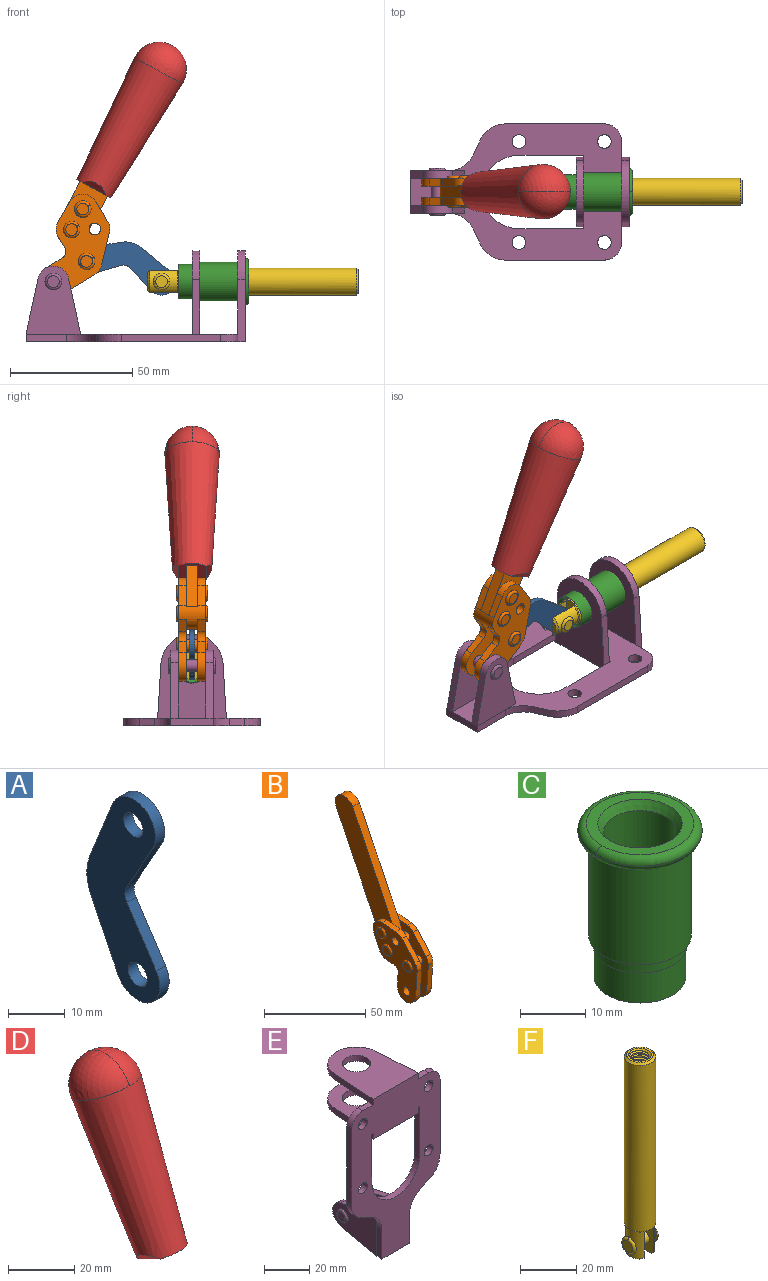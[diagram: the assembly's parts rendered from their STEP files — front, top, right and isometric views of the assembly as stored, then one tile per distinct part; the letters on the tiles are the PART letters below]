
ASSEMBLY  parts=6 mates=6
PART A: 12 faces, bbox 2.3x18.2x42.8 mm
  f0: cylinder r=2.4mm len=4.8mm, axis (1,0,0), area 34.9mm2, adj f4,f11
  f1: cylinder r=10.41mm len=8.47mm, axis (1,0,0), area 20.2mm2, adj f4,f9,f10,f11
  f2: cylinder r=3.05mm len=3.16mm, axis (1,0,0), area 7.7mm2, adj f4,f6,f7,f11
  f3: cylinder r=2.4mm len=4.8mm, axis (1,0,0), area 34.9mm2, adj f4,f11
  f4: plane 42.81x18.23mm, normal (-1,0,0), area 414.1mm2, adj f0,f1,f2,f3,f5,f6,f7,f8
  f5: cylinder r=5.54mm len=10.67mm, axis (1,0,0), area 41.8mm2, adj f4,f6,f10,f11
  f6: plane 11.66x6.53mm, normal (0,-0.87,-0.49), area 30.9mm2, adj f2,f4,f5,f11
  f7: plane 11.17x7.33mm, normal (0,-0.84,0.55), area 30.9mm2, adj f2,f4,f8,f11
  f8: cylinder r=5.54mm len=10.51mm, axis (1,0,0), area 41.8mm2, adj f4,f7,f9,f11
  f9: plane 13.67x6.67mm, normal (0,0.9,-0.44), area 35.1mm2, adj f1,f4,f8,f11
  f10: plane 14.1x5.7mm, normal (0,0.93,0.37), area 35.1mm2, adj f1,f4,f5,f11
  f11: plane 42.81x18.23mm, normal (1,0,0), area 414.1mm2, adj f0,f1,f2,f3,f5,f6,f7,f8
PART B: 59 faces, bbox 12.9x60.2x99.6 mm
  f0: torus R=2.39mm, axis (-1,0,0), area 14.9mm2, adj f20,f43,f51
  f1: torus R=2.39mm, axis (-1,0,0), area 14.9mm2, adj f19,f42,f51
  f2: torus R=2.39mm, axis (-1,0,0), area 14.9mm2, adj f18,f35,f51
  f3: torus R=2.39mm, axis (-1,0,0), area 14.9mm2, adj f14,f17,f23
  f4: torus R=2.39mm, axis (-1,0,0), area 14.9mm2, adj f13,f16,f23
  f5: torus R=2.39mm, axis (-1,0,0), area 14.9mm2, adj f12,f15,f23
  f6: cylinder r=2.39mm len=4.78mm, axis (1,0,0), area 46.5mm2, adj f48,f50,f51
  f7: cylinder r=2.39mm len=4.78mm, axis (1,0,0), area 46.5mm2, adj f50,f51
  f8: cylinder r=6.35mm len=12.68mm, axis (1,0,0), area 61.8mm2, adj f38,f39,f50,f51
  f9: cylinder r=2.39mm len=4.78mm, axis (-1,0,0), area 70.5mm2, adj f46,f50
  f10: cylinder r=2.39mm len=4.78mm, axis (-1,0,0), area 46.5mm2, adj f23,f45,f46
  f11: cylinder r=2.39mm len=4.78mm, axis (-1,0,0), area 46.5mm2, adj f23,f46
  f12: plane 4.78x4.78mm, normal (1,0,0), area 17.9mm2, adj f5,f15
  f13: plane 4.78x4.78mm, normal (1,0,0), area 17.9mm2, adj f4,f16
  f14: plane 4.78x4.78mm, normal (1,0,0), area 17.9mm2, adj f3,f17
  f15: torus R=2.39mm, axis (-1,0,0), area 14.9mm2, adj f5,f12,f23
  f16: torus R=2.39mm, axis (-1,0,0), area 14.9mm2, adj f4,f13,f23
  f17: torus R=2.39mm, axis (-1,0,0), area 14.9mm2, adj f3,f14,f23
  f18: plane 4.78x4.78mm, normal (-1,0,0), area 17.9mm2, adj f2,f35
  f19: plane 4.78x4.78mm, normal (-1,0,0), area 17.9mm2, adj f1,f42
  f20: plane 4.78x4.78mm, normal (-1,0,0), area 17.9mm2, adj f0,f43
  f21: plane 2.26x0.2mm, normal (1,0,0), area 0.2mm2, adj f31,f44
  f22: plane 2.26x0.2mm, normal (-1,0,0), area 0.2mm2, adj f41,f44
  f23: plane 39.37x30.77mm, normal (1,0,0), area 565.5mm2, adj f3,f4,f5,f10,f11,f15,f16,f17
  f24: cylinder r=6.1mm len=4.15mm, axis (-1,0,0), area 14.7mm2, adj f23,f25,f32,f46
  f25: plane 10.25x9.01mm, normal (0,-0.75,0.66), area 42.3mm2, adj f23,f24,f26,f46
  f26: cylinder r=6.35mm len=4.64mm, axis (-1,0,0), area 15.6mm2, adj f23,f25,f27,f46
  f27: plane 15.84x3.1mm, normal (0,-1,-0.07), area 49.2mm2, adj f23,f26,f28,f46
  f28: cylinder r=6.35mm len=12.68mm, axis (-1,0,0), area 61.8mm2, adj f23,f27,f29,f46
  f29: plane 8.11x3.1mm, normal (0,1,0.07), area 25.2mm2, adj f23,f28,f30,f46
  f30: cylinder r=3.05mm len=3.25mm, axis (-1,0,0), area 14.8mm2, adj f23,f29,f31,f46
  f31: plane 5.99x3.1mm, normal (0,0.07,-1), area 18.6mm2, adj f21,f23,f30,f44,f46
  f32: plane 9.5x3.1mm, normal (0,-0.07,1), area 29.5mm2, adj f23,f24,f33,f46,f47
  f33: cylinder r=6.1mm len=8.63mm, axis (-1,0,0), area 39.1mm2, adj f23,f32,f34,f47
  f34: plane 8.65x3.96mm, normal (0,0.91,-0.42), area 29.5mm2, adj f23,f33,f44,f47
  f35: torus R=2.39mm, axis (-1,0,0), area 14.9mm2, adj f2,f18,f51
  f36: plane 10.25x9.01mm, normal (0,-0.75,0.66), area 42.3mm2, adj f37,f49,f50,f51
  f37: cylinder r=6.35mm len=4.64mm, axis (1,0,0), area 15.6mm2, adj f36,f38,f50,f51
  f38: plane 15.84x3.1mm, normal (0,-1,-0.07), area 49.2mm2, adj f8,f37,f50,f51
  f39: plane 8.11x3.1mm, normal (0,1,0.07), area 25.2mm2, adj f8,f40,f50,f51
  f40: cylinder r=3.05mm len=3.25mm, axis (1,0,0), area 14.8mm2, adj f39,f41,f50,f51
  f41: plane 5.99x3.1mm, normal (0,0.07,-1), area 18.6mm2, adj f22,f40,f44,f50,f51
  f42: torus R=2.39mm, axis (-1,0,0), area 14.9mm2, adj f1,f19,f51
  f43: torus R=2.39mm, axis (-1,0,0), area 14.9mm2, adj f0,f20,f51
  f44: cylinder r=6.35mm len=12.12mm, axis (-1,0,0), area 128.9mm2, adj f21,f22,f23,f31,f34,f41,f46,f47
  f45: plane 2.65x1.35mm, normal (1,0,0), area 1mm2, adj f10,f55
  f46: plane 39.08x20.42mm, normal (-1,0,0), area 412.5mm2, adj f9,f10,f11,f24,f25,f26,f27,f28
  f47: plane 77.62x39.82mm, normal (1,0,0), area 850mm2, adj f32,f33,f34,f44,f53,f54,f55
  f48: plane 2.65x1.35mm, normal (-1,0,0), area 1mm2, adj f6,f55
  f49: cylinder r=6.1mm len=4.15mm, axis (1,0,0), area 14.7mm2, adj f36,f50,f51,f56
  f50: plane 39.08x20.42mm, normal (1,0,0), area 412.5mm2, adj f6,f7,f8,f9,f36,f37,f38,f39
  f51: plane 39.37x30.77mm, normal (-1,0,0), area 565.5mm2, adj f0,f1,f2,f6,f7,f8,f35,f36
  f52: plane 8.65x3.96mm, normal (0,0.91,-0.42), area 29.5mm2, adj f44,f51,f57,f58
  f53: plane 68.49x33.4mm, normal (0,0.9,-0.44), area 358.1mm2, adj f44,f47,f54,f58
  f54: cylinder r=6.35mm len=12.06mm, axis (1,0,0), area 93.7mm2, adj f47,f53,f55,f58
  f55: plane 68.49x33.4mm, normal (0,-0.9,0.44), area 358.1mm2, adj f44,f45,f46,f47,f48,f50,f54,f58
  f56: plane 9.5x3.1mm, normal (0,-0.07,1), area 29.5mm2, adj f49,f50,f51,f57,f58
  f57: cylinder r=6.1mm len=8.63mm, axis (1,0,0), area 39.1mm2, adj f51,f52,f56,f58
  f58: plane 77.62x39.82mm, normal (-1,0,0), area 850mm2, adj f44,f52,f53,f54,f55,f56,f57
PART C: 15 faces, bbox 20.6x20.6x28.7 mm
  f0: torus R=8.26mm, axis (0,0,1), area 56.8mm2, adj f1,f10,f12
  f1: torus R=8.26mm, axis (0,0,1), area 56.8mm2, adj f0,f6,f13
  f2: cylinder r=5.59mm len=25.91mm, axis (0,0,1), area 909.6mm2, adj f3,f4
  f3: cone r=6.86mm half-angle=45deg, axis (0,0,-1), area 70.2mm2, adj f2,f14
  f4: cone r=6.47mm half-angle=30deg, axis (0,0,1), area 66.7mm2, adj f2,f13
  f5: cylinder r=7.04mm len=14.07mm, axis (0,0,1), area 252.6mm2, adj f11,f14
  f6: torus R=8.26mm, axis (0,0,1), area 56.8mm2, adj f1,f12,f13
  f7: cylinder r=7.16mm len=14.33mm, axis (0,0,1), area 91.5mm2, adj f9,f11
  f8: cylinder r=7.86mm len=18.42mm, axis (0,0,1), area 909.6mm2, adj f9,f10
  f9: plane 15.72x15.72mm, normal (0,0,-1), area 33mm2, adj f7,f8
  f10: plane 16.51x16.51mm, normal (0,0,-1), area 19.9mm2, adj f0,f8,f12
  f11: plane 14.33x14.33mm, normal (0,0,-1), area 5.7mm2, adj f5,f7
  f12: torus R=8.26mm, axis (0,0,1), area 56.8mm2, adj f0,f6,f10
  f13: plane 16.51x16.51mm, normal (0,0,1), area 82.7mm2, adj f1,f4,f6
  f14: plane 14.07x14.07mm, normal (0,0,-1), area 7.8mm2, adj f3,f5
PART D: 11 faces, bbox 22.3x42.6x64.5 mm
  f0: sphere r=11.13mm, area 411.4mm2, adj f1,f8
  f1: cone r=11.11mm half-angle=3.3deg, axis (0,0.44,0.9), area 3251.8mm2, adj f0,f7,f8,f9,f10
  f2: cylinder r=6.16mm len=11.7mm, axis (1,0,0), area 89.5mm2, adj f3,f4,f5,f6
  f3: plane 60.23x36.75mm, normal (-1,0,0), area 763.6mm2, adj f2,f4,f6,f10
  f4: plane 51.37x25.05mm, normal (0,0.9,-0.44), area 264.2mm2, adj f2,f3,f5,f10
  f5: plane 60.23x36.75mm, normal (1,0,0), area 763.6mm2, adj f2,f4,f6,f10
  f6: plane 51.37x25.05mm, normal (0,-0.9,0.44), area 264.2mm2, adj f2,f3,f5,f10
  f7: plane 9.95x5.95mm, normal (0.71,-0.31,-0.64), area 25.8mm2, adj f1,f10
  f8: sphere r=11.13mm, area 411.4mm2, adj f0,f1
  f9: plane 9.95x5.95mm, normal (-0.71,-0.31,-0.64), area 25.8mm2, adj f1,f10
  f10: plane 14.27x11.38mm, normal (0,-0.44,-0.9), area 106.7mm2, adj f1,f3,f4,f5,f6,f7,f9
PART E: 55 faces, bbox 55.7x37.4x89.8 mm
  f0: torus R=2.41mm, axis (-1,0,0), area 15mm2, adj f11,f15,f25
  f1: torus R=2.41mm, axis (-1,0,0), area 15mm2, adj f10,f12,f22
  f2: cylinder r=2.78mm len=5.56mm, axis (0,-1,0), area 54.2mm2, adj f30,f54
  f3: cylinder r=14.99mm len=29.97mm, axis (0,-1,0), area 145.9mm2, adj f30,f49,f53,f54
  f4: cylinder r=2.78mm len=5.56mm, axis (0,-1,0), area 54.2mm2, adj f30,f54
  f5: cylinder r=2.78mm len=5.56mm, axis (0,-1,0), area 54.2mm2, adj f30,f54
  f6: cylinder r=2.78mm len=5.56mm, axis (0,-1,0), area 54.2mm2, adj f30,f54
  f7: cylinder r=6.35mm len=12.7mm, axis (0,0,1), area 123.6mm2, adj f27,f51
  f8: cylinder r=6.35mm len=12.7mm, axis (0,0,-1), area 124.7mm2, adj f21,f35
  f9: cylinder r=2.41mm len=11.18mm, axis (-1,0,0), area 169.4mm2, adj f16,f19
  f10: plane 4.83x4.83mm, normal (1,0,0), area 18.3mm2, adj f1,f12
  f11: plane 4.83x4.83mm, normal (-1,0,0), area 18.3mm2, adj f0,f15
  f12: torus R=2.41mm, axis (-1,0,0), area 15mm2, adj f1,f10,f22
  f13: cylinder r=6.35mm len=12.41mm, axis (1,0,0), area 53.4mm2, adj f18,f19,f22,f23
  f14: cylinder r=6.35mm len=12.41mm, axis (-1,0,0), area 53.4mm2, adj f16,f17,f24,f25
  f15: torus R=2.41mm, axis (-1,0,0), area 15mm2, adj f0,f11,f25
  f16: plane 27.86x22.35mm, normal (1,0,0), area 425.4mm2, adj f9,f14,f17,f24,f30
  f17: plane 22.86x4.97mm, normal (0,0.21,0.98), area 72.5mm2, adj f14,f16,f25,f30
  f18: plane 22.86x4.97mm, normal (0,0.21,0.98), area 72.5mm2, adj f13,f19,f22,f30
  f19: plane 27.86x22.35mm, normal (-1,0,0), area 425.4mm2, adj f9,f13,f18,f23,f30
  f20: cylinder r=12.7mm len=25.35mm, axis (0,0,-1), area 119.8mm2, adj f21,f34,f35,f36
  f21: plane 34.21x28.07mm, normal (0,0,-1), area 702.4mm2, adj f8,f20,f30,f34,f36
  f22: plane 27.96x22.45mm, normal (1,0,0), area 407.2mm2, adj f1,f12,f13,f18,f23,f30,f42,f43
  f23: plane 22.86x4.97mm, normal (0,0.21,-0.98), area 72.5mm2, adj f13,f19,f22,f44
  f24: plane 22.86x4.97mm, normal (0,0.21,-0.98), area 72.5mm2, adj f14,f16,f25,f44
  f25: plane 27.86x22.35mm, normal (-1,0,0), area 407.1mm2, adj f0,f14,f15,f17,f24,f30,f45,f46
  f26: plane 3.1x0.95mm, normal (0,0,-1), area 2.7mm2, adj f30,f49,f50,f54
  f27: plane 34.21x28.07mm, normal (0,0,1), area 702.4mm2, adj f7,f28,f30,f50,f52
  f28: cylinder r=12.7mm len=25.35mm, axis (0,0,1), area 118.8mm2, adj f27,f50,f51,f52
  f29: plane 3.1x0.95mm, normal (0,0,-1), area 2.7mm2, adj f30,f52,f53,f54
  f30: plane 86.54x55.63mm, normal (0,1,0), area 2362.9mm2, adj f2,f3,f4,f5,f6,f16,f17,f18
  f31: plane 40.56x3.1mm, normal (-1,0,0), area 125.7mm2, adj f30,f32,f48,f54
  f32: cylinder r=7.11mm len=7.11mm, axis (0,-1,0), area 34.6mm2, adj f30,f31,f33,f54
  f33: plane 6.67x3.1mm, normal (0,0,1), area 20.4mm2, adj f30,f32,f34,f54
  f34: plane 25.39x3.13mm, normal (-1,0.06,0), area 79.5mm2, adj f20,f21,f33,f35,f54
  f35: plane 37.31x28.45mm, normal (0,0,1), area 789.9mm2, adj f8,f20,f34,f36,f54
  f36: plane 25.39x3.13mm, normal (1,0.06,0), area 79.5mm2, adj f20,f21,f35,f37,f54
  f37: plane 6.67x3.1mm, normal (0,0,1), area 20.4mm2, adj f30,f36,f38,f54
  f38: cylinder r=7.11mm len=7.11mm, axis (0,-1,0), area 34.6mm2, adj f30,f37,f39,f54
  f39: plane 40.56x3.1mm, normal (1,0,0), area 125.7mm2, adj f30,f38,f40,f54
  f40: cylinder r=11.18mm len=10.16mm, axis (0,-1,0), area 39.5mm2, adj f30,f39,f41,f54
  f41: plane 6.09x3.1mm, normal (0.42,0,-0.91), area 20.8mm2, adj f30,f40,f42,f54
  f42: cylinder r=11.18mm len=9.41mm, axis (0,-1,0), area 37.2mm2, adj f22,f30,f41,f43,f54
  f43: plane 16.5x3.1mm, normal (1,0,0), area 51.1mm2, adj f22,f42,f44,f54
  f44: plane 17.37x3.1mm, normal (0,0,-1), area 53.8mm2, adj f23,f24,f30,f43,f45,f54
  f45: plane 16.5x3.1mm, normal (-1,0,0), area 51.1mm2, adj f25,f44,f46,f54
  f46: cylinder r=11.18mm len=9.41mm, axis (0,-1,0), area 37.2mm2, adj f25,f30,f45,f47,f54
  f47: plane 6.09x3.1mm, normal (-0.42,0,-0.91), area 20.8mm2, adj f30,f46,f48,f54
  f48: cylinder r=11.18mm len=10.16mm, axis (0,-1,0), area 39.5mm2, adj f30,f31,f47,f54
  f49: plane 26.54x3.1mm, normal (-1,0,0), area 82.3mm2, adj f3,f26,f30,f54
  f50: plane 25.39x3.1mm, normal (1,0.06,0), area 78.8mm2, adj f26,f27,f28,f51,f54
  f51: plane 37.31x28.45mm, normal (0,0,-1), area 789.9mm2, adj f7,f28,f50,f52,f54
  f52: plane 25.39x3.1mm, normal (-1,0.06,0), area 78.8mm2, adj f27,f28,f29,f51,f54
  f53: plane 26.54x3.1mm, normal (1,0,0), area 82.3mm2, adj f3,f29,f30,f54
  f54: plane 89.66x55.63mm, normal (0,-1,0), area 2678.5mm2, adj f2,f3,f4,f5,f6,f26,f29,f31
PART F: 48 faces, bbox 12.6x11.1x86.1 mm
  f0: torus R=2.41mm, axis (-1,0,0), area 15mm2, adj f30,f32,f34
  f1: torus R=2.41mm, axis (-1,0,0), area 15mm2, adj f29,f31,f33
  f2: cylinder r=5.54mm len=72.39mm, axis (0,0,1), area 2518.5mm2, adj f3,f4,f42,f43
  f3: cone r=5.54mm half-angle=45deg, axis (0,0,1), area 7.6mm2, adj f2,f5,f41
  f4: cone r=5.54mm half-angle=45deg, axis (0,0,-1), area 34.9mm2, adj f2,f39
  f5: cylinder r=5.08mm len=11.48mm, axis (0,0,1), area 108.3mm2, adj f3,f7,f8,f41
  f6: cylinder r=2.41mm len=4.83mm, axis (-1,0,0), area 71.2mm2, adj f40,f41
  f7: cylinder r=2.41mm len=4.83mm, axis (-1,0,0), area 7.6mm2, adj f5,f34
  f8: cone r=5.08mm half-angle=45deg, axis (0,0,1), area 10.6mm2, adj f5,f37,f41
  f9: cone r=3.98mm half-angle=45deg, axis (0,0,1), area 17.6mm2, adj f27,f39,f45,f46,f47
  f10: cylinder r=2.41mm len=4.83mm, axis (-1,0,0), area 7.6mm2, adj f33,f38
  f11: cylinder r=3.2mm len=6.4mm, axis (0,0,1), area 78.4mm2, adj f12,f28,f44,f45,f47
  f12: cylinder r=3.2mm len=6.4mm, axis (0,0,1), area 10.5mm2, adj f11,f13,f45,f47
  f13: cylinder r=3.2mm len=6.4mm, axis (0,0,1), area 10.5mm2, adj f12,f14,f45,f47
  f14: cylinder r=3.2mm len=6.4mm, axis (0,0,1), area 10.5mm2, adj f13,f15,f45,f47
  f15: cylinder r=3.2mm len=6.4mm, axis (0,0,1), area 10.5mm2, adj f14,f16,f45,f47
  f16: cylinder r=3.2mm len=6.4mm, axis (0,0,1), area 10.5mm2, adj f15,f17,f45,f47
  f17: cylinder r=3.2mm len=6.4mm, axis (0,0,1), area 10.5mm2, adj f16,f18,f45,f47
  f18: cylinder r=3.2mm len=6.4mm, axis (0,0,1), area 10.5mm2, adj f17,f19,f45,f47
  f19: cylinder r=3.2mm len=6.4mm, axis (0,0,1), area 10.5mm2, adj f18,f20,f45,f47
  f20: cylinder r=3.2mm len=6.4mm, axis (0,0,1), area 10.5mm2, adj f19,f21,f45,f47
  f21: cylinder r=3.2mm len=6.4mm, axis (0,0,1), area 10.5mm2, adj f20,f22,f45,f47
  f22: cylinder r=3.2mm len=6.4mm, axis (0,0,1), area 10.5mm2, adj f21,f23,f45,f47
  f23: cylinder r=3.2mm len=6.4mm, axis (0,0,1), area 10.5mm2, adj f22,f24,f45,f47
  f24: cylinder r=3.2mm len=6.4mm, axis (0,0,1), area 10.5mm2, adj f23,f25,f45,f47
  f25: cylinder r=3.2mm len=6.4mm, axis (0,0,1), area 10.5mm2, adj f24,f26,f45,f47
  f26: cylinder r=3.2mm len=6.4mm, axis (0,0,1), area 10.5mm2, adj f25,f27,f45,f47
  f27: cylinder r=3.2mm len=6.4mm, axis (0,0,1), area 7.4mm2, adj f9,f26,f45,f47
  f28: cone r=3.2mm half-angle=60deg, axis (0,0,1), area 37.2mm2, adj f11
  f29: plane 4.83x4.83mm, normal (-1,0,0), area 18.3mm2, adj f1,f31
  f30: plane 4.83x4.83mm, normal (1,0,0), area 18.3mm2, adj f0,f32
  f31: torus R=2.41mm, axis (-1,0,0), area 15mm2, adj f1,f29,f33
  f32: torus R=2.41mm, axis (-1,0,0), area 15mm2, adj f0,f30,f34
  f33: plane 6.83x6.83mm, normal (1,0,0), area 18.3mm2, adj f1,f10,f31
  f34: plane 6.83x6.83mm, normal (-1,0,0), area 18.3mm2, adj f0,f7,f32
  f35: cone r=5.08mm half-angle=45deg, axis (0,0,1), area 10.6mm2, adj f36,f38,f40
  f36: plane 7.25x1.97mm, normal (0,0,-1), area 10mm2, adj f35,f40
  f37: plane 7.25x1.97mm, normal (0,0,-1), area 10mm2, adj f8,f41
  f38: cylinder r=5.08mm len=11.48mm, axis (0,0,1), area 108.3mm2, adj f10,f35,f40,f42
  f39: plane 9.55x9.55mm, normal (0,0,1), area 22mm2, adj f4,f9
  f40: plane 12.76x10.09mm, normal (1,0,0), area 95.7mm2, adj f6,f35,f36,f38,f42,f43
  f41: plane 12.76x10.09mm, normal (-1,0,0), area 95.7mm2, adj f3,f5,f6,f8,f37,f43
  f42: cone r=5.54mm half-angle=45deg, axis (0,0,1), area 7.6mm2, adj f2,f38,f40
  f43: plane 11.07x4.7mm, normal (0,0,-1), area 50.4mm2, adj f2,f40,f41
  f44: plane 0.89x0.62mm, normal (-1,0,0), area 0.3mm2, adj f11,f45,f46,f47
  f45: bspline ~24.8x7.63mm, area 266.6mm2, adj f9,f11,f12,f13,f14,f15,f16,f17
  f46: bspline ~24.87x7.63mm, area 73.6mm2, adj f9,f44,f45,f47
  f47: bspline ~24.98x7.63mm, area 272.5mm2, adj f9,f11,f12,f13,f14,f15,f16,f17
PLACE A rot(axis=(0.53,-0.53,-0.66),112.8deg) t=(-47.22,-0.05,5.49)mm
PLACE B rot(axis=(0.42,0.42,0.81),102.2deg) t=(-29.87,-0.05,23.19)mm
PLACE C rot(axis=(0.71,0,0.71),180deg) t=(-39.46,24.56,24.71)mm
PLACE D rot(axis=(0.42,0.42,0.81),102.2deg) t=(-29.87,-0.09,23.19)mm
PLACE E rot(axis=(0.58,0.58,0.58),120deg) t=(-38.19,-0.05,0.1)mm fixed
PLACE F rot(axis=(0.58,0.58,0.58),120deg) t=(-41.54,-0.05,0.1)mm
MATE slider E.f7 <-> F.f2  axis (1,0,0) through (8.2,-0.05,24.71)mm
MATE revolute A.f5 <-> B.f4  axis (0,-1,0) through (-56.73,-0.05,32.96)mm
MATE fastened E.f7 <-> C.f2  axis (1,0,0) through (8.2,-0.05,24.71)mm
MATE revolute A.f3 <-> F.f6  axis (0,-1,0) through (-26.07,-0.05,24.71)mm
MATE fastened D.f2 <-> B.f54  axis (0,1,0) through (-26.26,-2.4,112.82)mm
MATE revolute B.f7 <-> E.f0  axis (0,-1,0) through (-70.29,-0.05,24.71)mm
